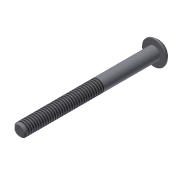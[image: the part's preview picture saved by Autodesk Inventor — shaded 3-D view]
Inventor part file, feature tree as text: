
AUTODESK INVENTOR PART (.ipt)
format: ipt  version: 2013 (Build 170138000, 138)  size: 108,544 bytes
history: native  units: in
note: dims shown in document units (in); Inventor stores cm internally (conversion verified against a paired STEP export)
features: sketch x3, extrude x2, revolve x1, chamfer x1, thread x1
ambient origin geometry x8: Origin, YZ Plane, XZ Plane, XY Plane, X Axis, Y Axis, Z Axis, Center Point
bodies: Solid1 (feature_tree)
feature tree (8):
  extrude  "Extrusion1"  Depth=1.75in TaperAngle=0.0deg
  revolve  "Revolution1"  [1 undecoded]
  extrude  "Extrusion2"  Depth=0.0938in
  chamfer  "Chamfer1"  Distance=0.0625in
  thread  "Thread1"  [1 undecoded]
  sketch  "Sketch1"  dims[d0=0.164in d1=1.75in d2=0.0in]
  sketch  "Sketch2"  dims[d3=0.087in d6=0.08in]
  sketch  "Sketch3"  dims[d7=90.0deg d8=0.0938in d9=0.0625in d10=0.0in d13=0.02in d14=0.125in d15=45.0deg d16=1.0in d17=0.0in d19=0.156in]
note: 2 required parameter values undecoded (feature->parameter linkage not recoverable at this tier; creation-order binding heuristic only, values carry confidence <= 0.55)